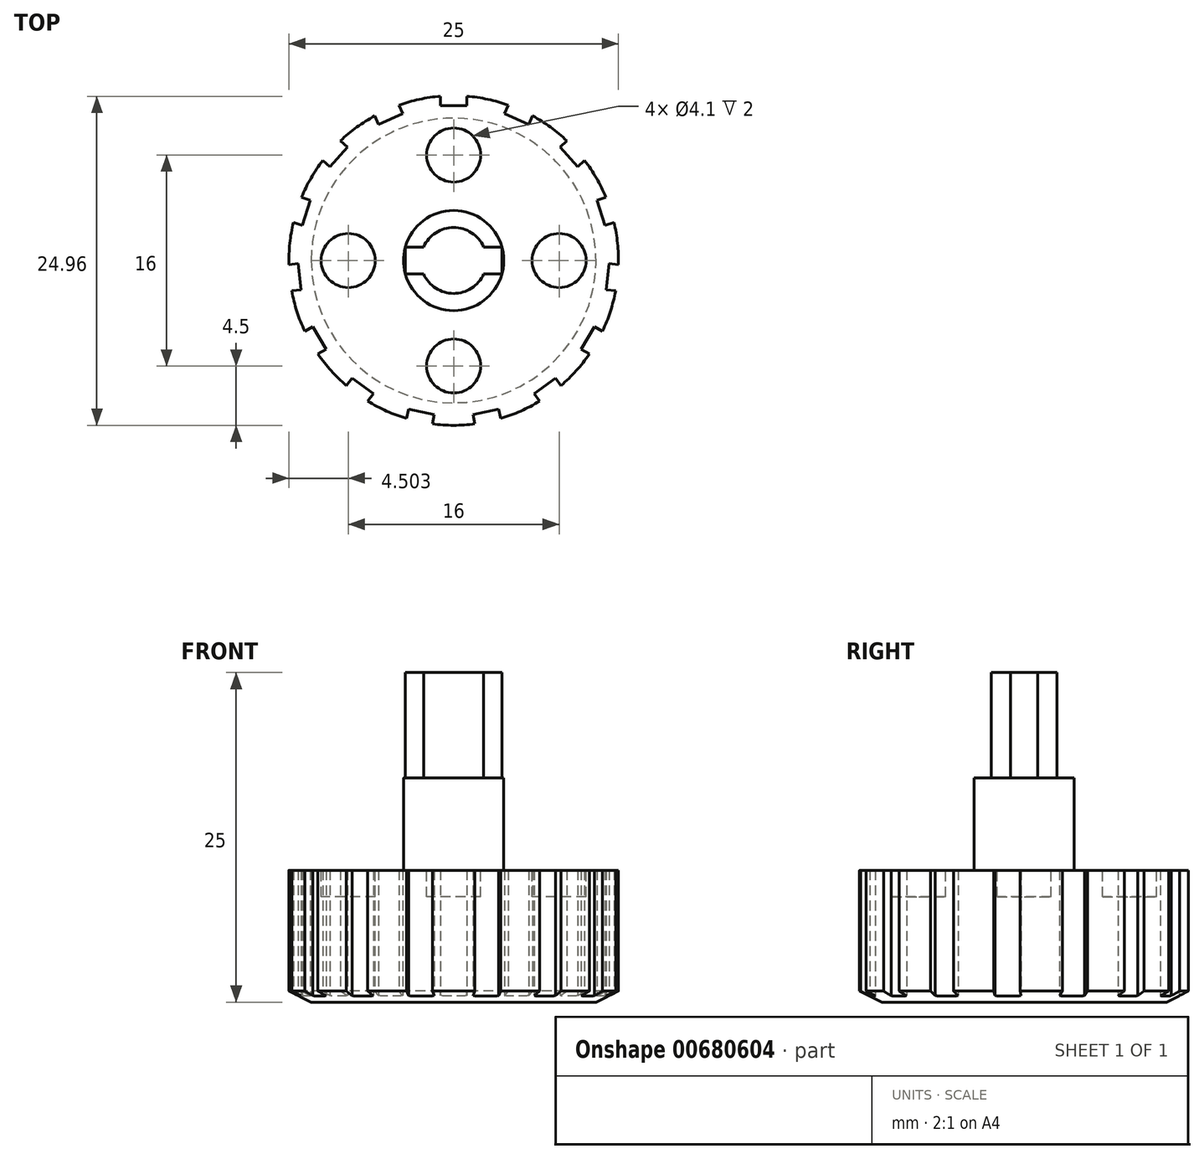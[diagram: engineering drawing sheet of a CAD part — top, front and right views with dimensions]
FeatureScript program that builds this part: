
annotation { "Feature Type Name" : "Feature", "Feature Type Description" : "" }
export const myFeature = defineFeature(function(context is Context, id is Id, definition is map)
    precondition{}
    {
        {
            var Q0;
            Q0=qCreatedBy(makeId("Top.planeOp"),FACE);
            var sketch = newSketch(context, id + "F0", { "sketchPlane" : qUnion([Q0])});
            skCircle(sketch, "E0", {"center": v(0, 0) * mm, "radius": 12.5 * mm});
            skLineSegment(sketch, "E1.bottom", {"start": v(1, 11.75) * mm, "end": v(-1, 11.75) * mm});
            skLineSegment(sketch, "E1.top", {"start": v(1, 13.25) * mm, "end": v(-1, 13.25) * mm});
            skLineSegment(sketch, "E1.left", {"start": v(1, 11.75) * mm, "end": v(1, 13.25) * mm});
            skLineSegment(sketch, "E1.right", {"start": v(-1, 11.75) * mm, "end": v(-1, 13.25) * mm});
            skPoint(sketch, "E1.middle", {"position": v(0, 12.5) * mm});
            skLineSegment(sketch, "E2.1.0", {"start": v(-3.87, 11.14) * mm, "end": v(-4.48, 12.51) * mm});
            skLineSegment(sketch, "E2.1.1", {"start": v(-4.48, 12.51) * mm, "end": v(-6.3, 11.7) * mm});
            skLineSegment(sketch, "E2.1.2", {"start": v(-3.87, 11.14) * mm, "end": v(-5.7, 10.33) * mm});
            skLineSegment(sketch, "E2.1.3", {"start": v(-5.7, 10.33) * mm, "end": v(-6.3, 11.7) * mm});
            skPoint(sketch, "E2.1.4", {"position": v(-5.08, 11.42) * mm});
            skLineSegment(sketch, "E2.2.0", {"start": v(-8.06, 8.6) * mm, "end": v(-9.18, 9.6) * mm});
            skLineSegment(sketch, "E2.2.1", {"start": v(-9.18, 9.6) * mm, "end": v(-10.52, 8.12) * mm});
            skLineSegment(sketch, "E2.2.2", {"start": v(-8.06, 8.6) * mm, "end": v(-9.4, 7.12) * mm});
            skLineSegment(sketch, "E2.2.3", {"start": v(-9.4, 7.12) * mm, "end": v(-10.52, 8.12) * mm});
            skPoint(sketch, "E2.2.4", {"position": v(-9.29, 8.36) * mm});
            skLineSegment(sketch, "E2.3.0", {"start": v(-10.87, 4.58) * mm, "end": v(-12.3, 5.05) * mm});
            skLineSegment(sketch, "E2.3.1", {"start": v(-12.3, 5.05) * mm, "end": v(-12.91, 3.14) * mm});
            skLineSegment(sketch, "E2.3.2", {"start": v(-10.87, 4.58) * mm, "end": v(-11.48, 2.68) * mm});
            skLineSegment(sketch, "E2.3.3", {"start": v(-11.48, 2.68) * mm, "end": v(-12.91, 3.14) * mm});
            skPoint(sketch, "E2.3.4", {"position": v(-11.89, 3.86) * mm});
            skLineSegment(sketch, "E2.4.0", {"start": v(-11.8, -0.23) * mm, "end": v(-13.28, -0.4) * mm});
            skLineSegment(sketch, "E2.4.1", {"start": v(-13.28, -0.4) * mm, "end": v(-13.07, -2.38) * mm});
            skLineSegment(sketch, "E2.4.2", {"start": v(-11.8, -0.23) * mm, "end": v(-11.58, -2.22) * mm});
            skLineSegment(sketch, "E2.4.3", {"start": v(-11.58, -2.22) * mm, "end": v(-13.07, -2.38) * mm});
            skPoint(sketch, "E2.4.4", {"position": v(-12.43, -1.3) * mm});
            skLineSegment(sketch, "E2.5.0", {"start": v(-10.68, -5) * mm, "end": v(-11.97, -5.76) * mm});
            skLineSegment(sketch, "E2.5.1", {"start": v(-11.97, -5.76) * mm, "end": v(-10.97, -7.5) * mm});
            skLineSegment(sketch, "E2.5.2", {"start": v(-10.68, -5) * mm, "end": v(-9.68, -6.74) * mm});
            skLineSegment(sketch, "E2.5.3", {"start": v(-9.68, -6.74) * mm, "end": v(-10.97, -7.5) * mm});
            skPoint(sketch, "E2.5.4", {"position": v(-10.83, -6.25) * mm});
            skLineSegment(sketch, "E2.6.0", {"start": v(-7.72, -8.92) * mm, "end": v(-8.6, -10.13) * mm});
            skLineSegment(sketch, "E2.6.1", {"start": v(-8.6, -10.13) * mm, "end": v(-6.98, -11.3) * mm});
            skLineSegment(sketch, "E2.6.2", {"start": v(-7.72, -8.92) * mm, "end": v(-6.1, -10.1) * mm});
            skLineSegment(sketch, "E2.6.3", {"start": v(-6.1, -10.1) * mm, "end": v(-6.98, -11.3) * mm});
            skPoint(sketch, "E2.6.4", {"position": v(-7.35, -10.11) * mm});
            skLineSegment(sketch, "E2.7.0", {"start": v(-3.42, -11.29) * mm, "end": v(-3.73, -12.75) * mm});
            skLineSegment(sketch, "E2.7.1", {"start": v(-3.73, -12.75) * mm, "end": v(-1.78, -13.17) * mm});
            skLineSegment(sketch, "E2.7.2", {"start": v(-3.42, -11.29) * mm, "end": v(-1.46, -11.7) * mm});
            skLineSegment(sketch, "E2.7.3", {"start": v(-1.46, -11.7) * mm, "end": v(-1.78, -13.17) * mm});
            skPoint(sketch, "E2.7.4", {"position": v(-2.6, -12.23) * mm});
            skLineSegment(sketch, "E2.8.0", {"start": v(1.46, -11.7) * mm, "end": v(1.78, -13.17) * mm});
            skLineSegment(sketch, "E2.8.1", {"start": v(1.78, -13.17) * mm, "end": v(3.73, -12.75) * mm});
            skLineSegment(sketch, "E2.8.2", {"start": v(1.46, -11.7) * mm, "end": v(3.42, -11.29) * mm});
            skLineSegment(sketch, "E2.8.3", {"start": v(3.42, -11.29) * mm, "end": v(3.73, -12.75) * mm});
            skPoint(sketch, "E2.8.4", {"position": v(2.6, -12.23) * mm});
            skLineSegment(sketch, "E2.9.0", {"start": v(6.1, -10.1) * mm, "end": v(6.98, -11.3) * mm});
            skLineSegment(sketch, "E2.9.1", {"start": v(6.98, -11.3) * mm, "end": v(8.6, -10.13) * mm});
            skLineSegment(sketch, "E2.9.2", {"start": v(6.1, -10.1) * mm, "end": v(7.72, -8.92) * mm});
            skLineSegment(sketch, "E2.9.3", {"start": v(7.72, -8.92) * mm, "end": v(8.6, -10.13) * mm});
            skPoint(sketch, "E2.9.4", {"position": v(7.35, -10.11) * mm});
            skLineSegment(sketch, "E2.10.0", {"start": v(9.68, -6.74) * mm, "end": v(10.97, -7.5) * mm});
            skLineSegment(sketch, "E2.10.1", {"start": v(10.97, -7.5) * mm, "end": v(11.97, -5.76) * mm});
            skLineSegment(sketch, "E2.10.2", {"start": v(9.68, -6.74) * mm, "end": v(10.68, -5) * mm});
            skLineSegment(sketch, "E2.10.3", {"start": v(10.68, -5) * mm, "end": v(11.97, -5.76) * mm});
            skPoint(sketch, "E2.10.4", {"position": v(10.83, -6.25) * mm});
            skLineSegment(sketch, "E2.11.0", {"start": v(11.58, -2.22) * mm, "end": v(13.07, -2.38) * mm});
            skLineSegment(sketch, "E2.11.1", {"start": v(13.07, -2.38) * mm, "end": v(13.28, -0.4) * mm});
            skLineSegment(sketch, "E2.11.2", {"start": v(11.58, -2.22) * mm, "end": v(11.8, -0.23) * mm});
            skLineSegment(sketch, "E2.11.3", {"start": v(11.8, -0.23) * mm, "end": v(13.28, -0.4) * mm});
            skPoint(sketch, "E2.11.4", {"position": v(12.43, -1.3) * mm});
            skLineSegment(sketch, "E2.12.0", {"start": v(11.48, 2.68) * mm, "end": v(12.91, 3.14) * mm});
            skLineSegment(sketch, "E2.12.1", {"start": v(12.91, 3.14) * mm, "end": v(12.3, 5.05) * mm});
            skLineSegment(sketch, "E2.12.2", {"start": v(11.48, 2.68) * mm, "end": v(10.87, 4.58) * mm});
            skLineSegment(sketch, "E2.12.3", {"start": v(10.87, 4.58) * mm, "end": v(12.3, 5.05) * mm});
            skPoint(sketch, "E2.12.4", {"position": v(11.89, 3.86) * mm});
            skLineSegment(sketch, "E2.13.0", {"start": v(9.4, 7.12) * mm, "end": v(10.52, 8.12) * mm});
            skLineSegment(sketch, "E2.13.1", {"start": v(10.52, 8.12) * mm, "end": v(9.18, 9.6) * mm});
            skLineSegment(sketch, "E2.13.2", {"start": v(9.4, 7.12) * mm, "end": v(8.06, 8.6) * mm});
            skLineSegment(sketch, "E2.13.3", {"start": v(8.06, 8.6) * mm, "end": v(9.18, 9.6) * mm});
            skPoint(sketch, "E2.13.4", {"position": v(9.29, 8.36) * mm});
            skLineSegment(sketch, "E2.14.0", {"start": v(5.7, 10.33) * mm, "end": v(6.3, 11.7) * mm});
            skLineSegment(sketch, "E2.14.1", {"start": v(6.3, 11.7) * mm, "end": v(4.48, 12.51) * mm});
            skLineSegment(sketch, "E2.14.2", {"start": v(5.7, 10.33) * mm, "end": v(3.87, 11.14) * mm});
            skLineSegment(sketch, "E2.14.3", {"start": v(3.87, 11.14) * mm, "end": v(4.48, 12.51) * mm});
            skPoint(sketch, "E2.14.4", {"position": v(5.08, 11.42) * mm});
            skSolve(sketch);
        }
        {
            var Q0;
            {var subQ75=sQuery(id+"F0.wireOp",EDGE,"E1.bottom");Q0=makeQuery(id+"F0.imprint","IMPRINT",FACE,{"disambiguationData":[TD([[makeQuery(id+"F0.imprint","IMPRINT",EDGE,{"derivedFrom":subQ75}),1.0]])]});}
            extrude(context, id + "F1", {"entities" : qUnion([Q0]), "depth" : 10 * mm, "offsetDistance" : 25 * mm});
        }
        {
            var Q0;
            Q0=makeQuery(id+"F1.opExtrude","CAP_FACE",FACE,{"disambiguationData":[OSD([sQuery(id+"F0.wireOp",EDGE,"E0"),sQuery(id+"F0.wireOp",EDGE,"E1.bottom"),sQuery(id+"F0.wireOp",EDGE,"E1.left"),sQuery(id+"F0.wireOp",EDGE,"E1.right"),sQuery(id+"F0.wireOp",EDGE,"E2.1.0"),sQuery(id+"F0.wireOp",EDGE,"E2.1.2"),sQuery(id+"F0.wireOp",EDGE,"E2.1.3"),sQuery(id+"F0.wireOp",EDGE,"E2.2.0"),sQuery(id+"F0.wireOp",EDGE,"E2.2.2"),sQuery(id+"F0.wireOp",EDGE,"E2.2.3"),sQuery(id+"F0.wireOp",EDGE,"E2.3.0"),sQuery(id+"F0.wireOp",EDGE,"E2.3.2"),sQuery(id+"F0.wireOp",EDGE,"E2.3.3"),sQuery(id+"F0.wireOp",EDGE,"E2.4.0"),sQuery(id+"F0.wireOp",EDGE,"E2.4.2"),sQuery(id+"F0.wireOp",EDGE,"E2.4.3"),sQuery(id+"F0.wireOp",EDGE,"E2.5.0"),sQuery(id+"F0.wireOp",EDGE,"E2.5.2"),sQuery(id+"F0.wireOp",EDGE,"E2.5.3"),sQuery(id+"F0.wireOp",EDGE,"E2.6.0"),sQuery(id+"F0.wireOp",EDGE,"E2.6.2"),sQuery(id+"F0.wireOp",EDGE,"E2.6.3"),sQuery(id+"F0.wireOp",EDGE,"E2.7.0"),sQuery(id+"F0.wireOp",EDGE,"E2.7.2"),sQuery(id+"F0.wireOp",EDGE,"E2.7.3"),sQuery(id+"F0.wireOp",EDGE,"E2.8.0"),sQuery(id+"F0.wireOp",EDGE,"E2.8.2"),sQuery(id+"F0.wireOp",EDGE,"E2.8.3"),sQuery(id+"F0.wireOp",EDGE,"E2.9.0"),sQuery(id+"F0.wireOp",EDGE,"E2.9.2"),sQuery(id+"F0.wireOp",EDGE,"E2.9.3"),sQuery(id+"F0.wireOp",EDGE,"E2.10.0"),sQuery(id+"F0.wireOp",EDGE,"E2.10.2"),sQuery(id+"F0.wireOp",EDGE,"E2.10.3"),sQuery(id+"F0.wireOp",EDGE,"E2.11.0"),sQuery(id+"F0.wireOp",EDGE,"E2.11.2"),sQuery(id+"F0.wireOp",EDGE,"E2.11.3"),sQuery(id+"F0.wireOp",EDGE,"E2.12.0"),sQuery(id+"F0.wireOp",EDGE,"E2.12.2"),sQuery(id+"F0.wireOp",EDGE,"E2.12.3"),sQuery(id+"F0.wireOp",EDGE,"E2.13.0"),sQuery(id+"F0.wireOp",EDGE,"E2.13.2"),sQuery(id+"F0.wireOp",EDGE,"E2.13.3"),sQuery(id+"F0.wireOp",EDGE,"E2.14.0"),sQuery(id+"F0.wireOp",EDGE,"E2.14.2"),sQuery(id+"F0.wireOp",EDGE,"E2.14.3")])],"isStart":false});
            var sketch = newSketch(context, id + "F2", { "sketchPlane" : qUnion([Q0])});
            skCircle(sketch, "E3", {"center": v(0, 0) * mm, "radius": 3.8 * mm});
            skSolve(sketch);
        }
        {
            var Q0;
            Q0 = qSketchRegion(id + "F2", true);
            extrude(context, id + "F3", {"entities" : qUnion([Q0]), "operationType" : NewBodyOperationType.ADD, "depth" : 7 * mm, "offsetDistance" : 25 * mm});
        }
        {
            var Q0;
            Q0=makeQuery(id+"F3.opExtrude","CAP_FACE",FACE,{"disambiguationData":[OSD([sQuery(id+"F2.wireOp",EDGE,"E3")])],"isStart":false});
            var sketch = newSketch(context, id + "F4", { "sketchPlane" : qUnion([Q0])});
            skArc(sketch, "E4", {"start": v(-2.28, -1.03) * mm, "mid": v(0, -2.5) * mm, "end": v(2.28, -1.03) * mm});
            skLineSegment(sketch, "E5.bottom", {"start": v(3.66, -1.03) * mm, "end": v(2.28, -1.03) * mm});
            skLineSegment(sketch, "E5.top", {"start": v(3.66, 1.03) * mm, "end": v(2.28, 1.03) * mm});
            skLineSegment(sketch, "E5.left", {"start": v(3.66, -1.03) * mm, "end": v(3.66, 1.03) * mm});
            skLineSegment(sketch, "E5.right", {"start": v(-3.66, -1.03) * mm, "end": v(-3.66, 1.03) * mm});
            skArc(sketch, "E6.trimOffspring", {"start": v(2.28, 1.03) * mm, "mid": v(0, 2.5) * mm, "end": v(-2.28, 1.03) * mm});
            skLineSegment(sketch, "E7.trimOffspring", {"start": v(-2.28, 1.03) * mm, "end": v(-3.66, 1.03) * mm});
            skLineSegment(sketch, "E8.trimOffspring", {"start": v(-2.28, -1.03) * mm, "end": v(-3.66, -1.03) * mm});
            skSolve(sketch);
        }
        {
            var Q0;
            Q0 = qSketchRegion(id + "F4", true);
            extrude(context, id + "F5", {"entities" : qUnion([Q0]), "operationType" : NewBodyOperationType.ADD, "depth" : 8 * mm, "offsetDistance" : 25 * mm});
        }
        {
            var Q0;
            Q0=qCreatedBy(makeId("Front.planeOp"),FACE);
            var sketch = newSketch(context, id + "F6", { "sketchPlane" : qUnion([Q0])});
            skLineSegment(sketch, "E9", {"start": v(0, 32.51) * mm, "end": v(0, -25.52) * mm, "construction": true});
            skLineSegment(sketch, "E10", {"start": v(-14.88, 0) * mm, "end": v(-14.88, 2) * mm});
            skLineSegment(sketch, "E11", {"start": v(-14.88, 2) * mm, "end": v(-10.8, 0) * mm});
            skLineSegment(sketch, "E12", {"start": v(-10.8, 0) * mm, "end": v(-14.88, 0) * mm});
            skSolve(sketch);
        }
        {
            var Q0;
            Q0 = qSketchRegion(id + "F6", true);
            var Q1;
            Q1=sQuery(id+"F6.wireOp",EDGE,"E9");
            revolve(context, id + "F7", {"operationType" : NewBodyOperationType.REMOVE, "surfaceOperationType" : NewSurfaceOperationType.NEW, "entities" : qUnion([Q0]), "axis" : qUnion([Q1]), "revolveType" : RevolveType.FULL, "oppositeDirection" : true});
        }
        {
            var Q0;
            Q0=makeQuery(id+"F1.opExtrude","CAP_FACE",FACE,{"disambiguationData":[OSD([sQuery(id+"F0.wireOp",EDGE,"E0"),sQuery(id+"F0.wireOp",EDGE,"E1.bottom"),sQuery(id+"F0.wireOp",EDGE,"E1.left"),sQuery(id+"F0.wireOp",EDGE,"E1.right"),sQuery(id+"F0.wireOp",EDGE,"E2.1.0"),sQuery(id+"F0.wireOp",EDGE,"E2.1.2"),sQuery(id+"F0.wireOp",EDGE,"E2.1.3"),sQuery(id+"F0.wireOp",EDGE,"E2.2.0"),sQuery(id+"F0.wireOp",EDGE,"E2.2.2"),sQuery(id+"F0.wireOp",EDGE,"E2.2.3"),sQuery(id+"F0.wireOp",EDGE,"E2.3.0"),sQuery(id+"F0.wireOp",EDGE,"E2.3.2"),sQuery(id+"F0.wireOp",EDGE,"E2.3.3"),sQuery(id+"F0.wireOp",EDGE,"E2.4.0"),sQuery(id+"F0.wireOp",EDGE,"E2.4.2"),sQuery(id+"F0.wireOp",EDGE,"E2.4.3"),sQuery(id+"F0.wireOp",EDGE,"E2.5.0"),sQuery(id+"F0.wireOp",EDGE,"E2.5.2"),sQuery(id+"F0.wireOp",EDGE,"E2.5.3"),sQuery(id+"F0.wireOp",EDGE,"E2.6.0"),sQuery(id+"F0.wireOp",EDGE,"E2.6.2"),sQuery(id+"F0.wireOp",EDGE,"E2.6.3"),sQuery(id+"F0.wireOp",EDGE,"E2.7.0"),sQuery(id+"F0.wireOp",EDGE,"E2.7.2"),sQuery(id+"F0.wireOp",EDGE,"E2.7.3"),sQuery(id+"F0.wireOp",EDGE,"E2.8.0"),sQuery(id+"F0.wireOp",EDGE,"E2.8.2"),sQuery(id+"F0.wireOp",EDGE,"E2.8.3"),sQuery(id+"F0.wireOp",EDGE,"E2.9.0"),sQuery(id+"F0.wireOp",EDGE,"E2.9.2"),sQuery(id+"F0.wireOp",EDGE,"E2.9.3"),sQuery(id+"F0.wireOp",EDGE,"E2.10.0"),sQuery(id+"F0.wireOp",EDGE,"E2.10.2"),sQuery(id+"F0.wireOp",EDGE,"E2.10.3"),sQuery(id+"F0.wireOp",EDGE,"E2.11.0"),sQuery(id+"F0.wireOp",EDGE,"E2.11.2"),sQuery(id+"F0.wireOp",EDGE,"E2.11.3"),sQuery(id+"F0.wireOp",EDGE,"E2.12.0"),sQuery(id+"F0.wireOp",EDGE,"E2.12.2"),sQuery(id+"F0.wireOp",EDGE,"E2.12.3"),sQuery(id+"F0.wireOp",EDGE,"E2.13.0"),sQuery(id+"F0.wireOp",EDGE,"E2.13.2"),sQuery(id+"F0.wireOp",EDGE,"E2.13.3"),sQuery(id+"F0.wireOp",EDGE,"E2.14.0"),sQuery(id+"F0.wireOp",EDGE,"E2.14.2"),sQuery(id+"F0.wireOp",EDGE,"E2.14.3")])],"isStart":false});
            var sketch = newSketch(context, id + "F8", { "sketchPlane" : qUnion([Q0])});
            skCircle(sketch, "E13", {"center": v(-8, 0) * mm, "radius": 2.05 * mm});
            skCircle(sketch, "E14.1.0", {"center": v(0, -8) * mm, "radius": 2.05 * mm});
            skCircle(sketch, "E14.2.0", {"center": v(8, 0) * mm, "radius": 2.05 * mm});
            skCircle(sketch, "E14.3.0", {"center": v(0, 8) * mm, "radius": 2.05 * mm});
            skPoint(sketch, "E14.center", {"position": v(0, 0) * mm});
            skSolve(sketch);
        }
        {
            var Q0;
            Q0 = qSketchRegion(id + "F8", true);
            extrude(context, id + "F9", {"entities" : qUnion([Q0]), "operationType" : NewBodyOperationType.REMOVE, "oppositeDirection" : true, "depth" : 2 * mm, "offsetDistance" : 25 * mm});
        }
    });
